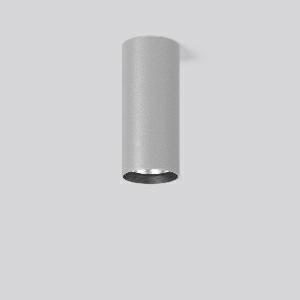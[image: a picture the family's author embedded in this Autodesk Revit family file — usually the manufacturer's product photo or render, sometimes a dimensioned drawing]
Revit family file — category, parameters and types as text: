
# Revit family: heledon_mini_a_931202_004_3_a787
name_source: partatom
category: Lighting Fixtures
units: mm (PartAtom-declared; Revit-internal decimal feet)

## family parameters
Cut with Voids When Loaded = No
Host = Face
Light Source = No
Part Type = Normal
Room Calculation Point = No
Round Connector Dimension = Use Diameter
Shared = No

## types (1)
- HELEDON mini A (1 x LED Modul 935, 2650 lm, 3500)
    Apparent Load = 20 VA
    Approval mark = CE
    CIE Flux Codes = 95 99 100 100 100
    Color Rendering = 92
    Color Temperature = 3500
    Default Elevation = 1800 mm
    Description = Series: HELEDON mini
Cylindrical surface-mounted downlight. Housing: die-cast aluminium, powder-coated. Internal ceiling frame polycarbonate with bayonet mounting. Black plastic ring and recessed LED to prevent glare from the side. Optical assembly with reflector made of MIRO-Silver with 98% total light reflection for outstanding efficiency - can be changed without tools. Best colour rendering index Ra>90. Suitable for Ceiling mounting. Easy installation with a separate ceiling frame with bayonet mounting and plug connection. Driver integrated. Connected via plug-in connector. High quality converter without flickering and stroboscopic effect. The following accessories can be mounted without use of tools: interchangeable lenses, decorative glasses, honeycomb louvre, clear and frosted diffusers, white interchangeable plastic ring. 
Colour: silver
Diameter: 87 mm
Height: 197 mm
Lamp: LED
Socket: without socket
Colour temperature: 3500K
Colour rendering index (CRI): 92
System power: 20 W
Rated luminous flux: 2650 lm
Luminous efficiency: 133 lm/W
Control gear: Regulated power supply
Protection class: I
Type of protection: IP 20
    Height = 197 mm
    Lamp = 1 x LED Modul 935
    Lamp Light Flux = 2650 lm
    Lamp count = 1
    Length = 87 mm
    Lifetime = 50000 h
    Luminous efficacy = 133 lm/W
    Manufacturer = RZB
    ModVariant = No
    Model = 931202.004.3
    Mounting Place = Ceiling
    Mounting Type = Surface mounted
    Number of Poles = 1
    OnlyDefault = Yes
    Power Factor = 1
    Product Name = HELEDON mini A
    Product group = Surface mounted downlights
    ProductGroupID = 302
    Protection Class = Protection class I
    Protection Degree = IP 20
    RLX_Detail_Level = 1
    RLX_Emergency_Light_Flux = 0 lm
    RLX_Emergency_Type = 0
    RLX_Emergency_Type_DB = No
    RlxData = <blob elided: 107525 chars, md5=8ea5fa15>
    Socket = socket
    Standby Power = 0 W
    System Light Flux = 2650 lm
    System Power = 20 W
    Type Comments = Product without accessories
    Type Image = 931188.004.jpg
    URL = http://relux.com
    VarID = ---
    Voltage = 230 V
    Voltage Range = 220-240 V
    Weight = 0.00 kg
    Width = 0 mm  [stored 0 ft]

note: [stored X ft] marks values corroborated as IEEE doubles in the binary element streams (Revit-internal decimal feet)

## geometry (parser evidence)
native form markers: Blend x4, Sweep x10
no freeform markers — native parametric forms only
